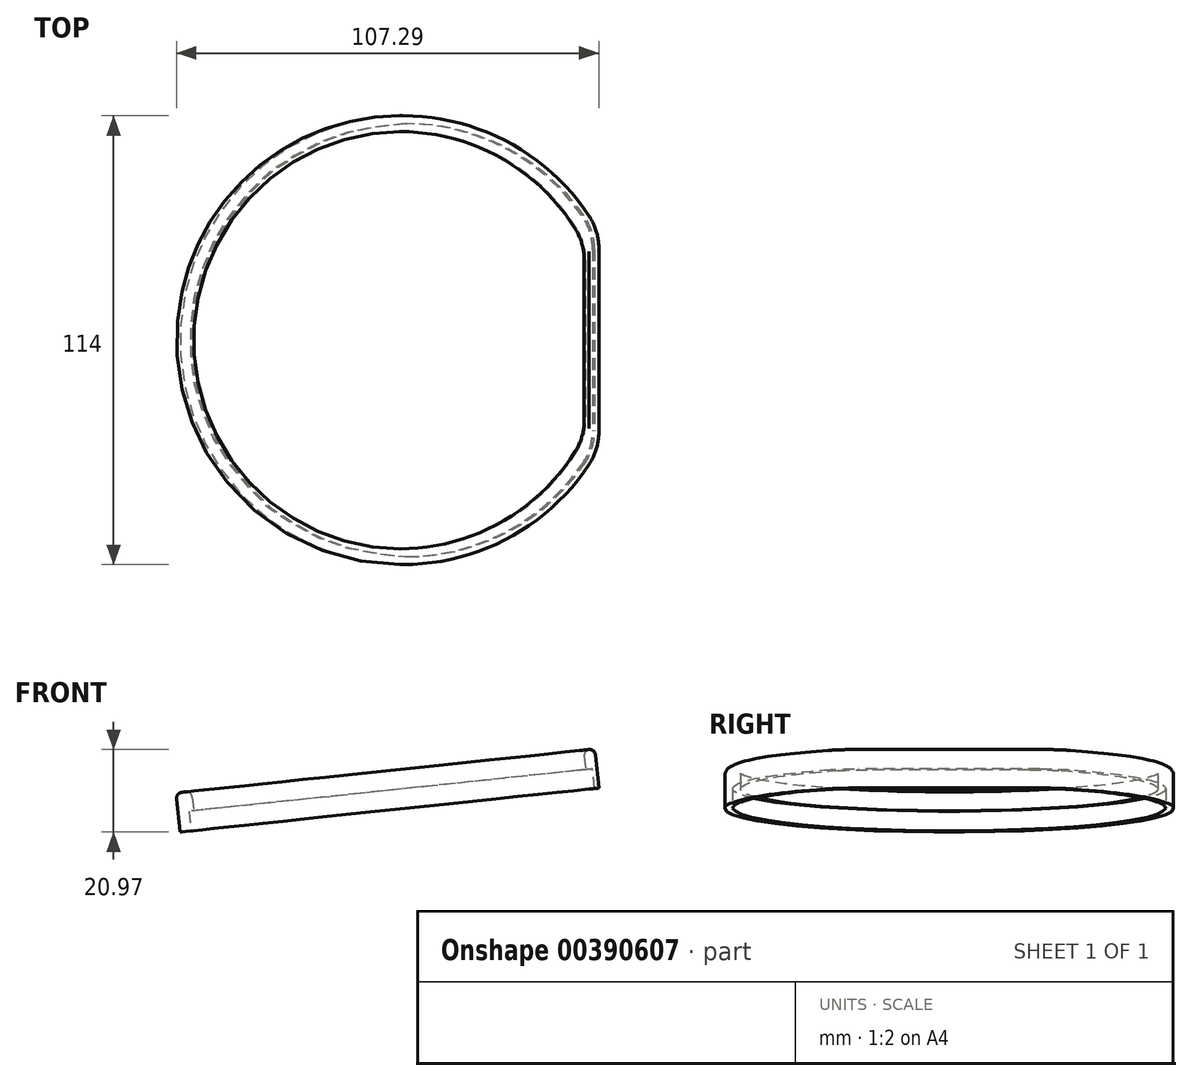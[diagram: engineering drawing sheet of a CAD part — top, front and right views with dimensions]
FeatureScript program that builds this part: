
annotation { "Feature Type Name" : "Feature", "Feature Type Description" : "" }
export const myFeature = defineFeature(function(context is Context, id is Id, definition is map)
    precondition{}
    {
        {
            var Q0;
            Q0=qCreatedBy(makeId("Front.planeOp"),FACE);
            var sketch = newSketch(context, id + "F0", { "sketchPlane" : qUnion([Q0])});
            skLineSegment(sketch, "E0", {"start": v(-46.94, 5.64) * mm, "end": v(44.02, 15.2) * mm, "construction": true});
            skLineSegment(sketch, "E1", {"start": v(-43.5, 0) * mm, "end": v(-43.5, 6) * mm, "construction": true});
            skLineSegment(sketch, "E2", {"start": v(43.5, 0) * mm, "end": v(43.5, 15.14) * mm, "construction": true});
            skLineSegment(sketch, "E3", {"start": v(-43.5, 0) * mm, "end": v(43.5, 0) * mm});
            skSolve(sketch);
        }
        {
            var Q0;
            Q0=sQuery(id+"F0.wireOp",EDGE,"E0");
            cPlane(context, id + "F1", {"entities" : qUnion([Q0]), "cplaneType" : CPlaneType.LINE_ANGLE, "offset" : 25 * mm, "angle" : 90 * degree, "width" : 150 * mm, "height" : 150 * mm});
        }
        {
            var Q0;
            Q0=qCreatedBy(id+"F1.planeOp",FACE);
            var sketch = newSketch(context, id + "F2", { "sketchPlane" : qUnion([Q0])});
            skCircle(sketch, "E4", {"center": v(0, 0) * mm, "radius": 53 * mm});
            skPoint(sketch, "E5", {"position": v(1, 0) * mm});
            skEllipse(sketch, "E6", {"center": v(1, 0) * mm, "majorRadius": 55.01 * mm, "minorRadius": 55.2 * mm, "majorAxis": v(0, 1)});
            skCircle(sketch, "E7", {"center": v(0, 0) * mm, "radius": 57 * mm});
            skLineSegment(sketch, "E8", {"start": v(48.86, 27.42) * mm, "end": v(48.86, -27.42) * mm});
            skLineSegment(sketch, "E9", {"start": v(47.12, 24.26) * mm, "end": v(47.12, -24.26) * mm});
            skLineSegment(sketch, "E10", {"start": v(49.98, -27.4) * mm, "end": v(49.98, 27.4) * mm});
            skSolve(sketch);
        }
        {
            var Q0;
            {var subQ4=sQuery(id+"F2.wireOp",EDGE,"E8");var subQ5=sQuery(id+"F2.wireOp",EDGE,"E6");var subQ7=makeQuery(id+"F2.imprint","INTERSECT",VERTEX,{"disambiguationData":[OD(1.0)],"derivedFrom":[subQ5,subQ4]});Q0=makeQuery(id+"F2.imprint","IMPRINT",FACE,{"disambiguationData":[TD([[makeQuery(id+"F2.imprint","IMPRINT",EDGE,{"disambiguationData":[TD([[subQ7,-1.0]])],"derivedFrom":subQ5}),-1.0]])]});}
            var Q1;
            {var subQ4=sQuery(id+"F2.wireOp",EDGE,"E9");var subQ5=sQuery(id+"F2.wireOp",EDGE,"E4");var subQ8=makeQuery(id+"F2.imprint","INTERSECT",VERTEX,{"disambiguationData":[OD(0.0)],"derivedFrom":[subQ5,subQ4]});Q1=makeQuery(id+"F2.imprint","IMPRINT",FACE,{"disambiguationData":[TD([[makeQuery(id+"F2.imprint","IMPRINT",EDGE,{"disambiguationData":[TD([[subQ8,1.0]])],"derivedFrom":subQ5}),-1.0]])]});}
            var Q2;
            {var subQ0=sQuery(id+"F2.wireOp",EDGE,"E9");Q2=makeQuery(id+"F2.imprint","IMPRINT",FACE,{"disambiguationData":[TD([[makeQuery(id+"F2.imprint","IMPRINT",EDGE,{"derivedFrom":subQ0}),1.0]])]});}
            var Q3;
            {var subQ0=sQuery(id+"F2.wireOp",EDGE,"E8");var subQ1=sQuery(id+"F2.wireOp",EDGE,"E4");var subQ2=makeQuery(id+"F2.imprint","INTERSECT",VERTEX,{"disambiguationData":[OD(0.0)],"derivedFrom":[subQ1,subQ0]});Q3=makeQuery(id+"F2.imprint","IMPRINT",FACE,{"disambiguationData":[TD([[makeQuery(id+"F2.imprint","IMPRINT",EDGE,{"disambiguationData":[TD([[subQ2,1.0]])],"derivedFrom":subQ1}),1.0]])]});}
            var Q4;
            {var subQ0=sQuery(id+"F2.wireOp",EDGE,"E8");var subQ1=sQuery(id+"F2.wireOp",EDGE,"E4");var subQ2=makeQuery(id+"F2.imprint","INTERSECT",VERTEX,{"disambiguationData":[OD(0.0)],"derivedFrom":[subQ1,subQ0]});Q4=makeQuery(id+"F2.imprint","IMPRINT",FACE,{"disambiguationData":[TD([[makeQuery(id+"F2.imprint","IMPRINT",EDGE,{"disambiguationData":[TD([[subQ2,1.0]])],"derivedFrom":subQ1}),-1.0]])]});}
            var Q5;
            {var subQ0=sQuery(id+"F2.wireOp",EDGE,"E8");var subQ1=sQuery(id+"F2.wireOp",EDGE,"E4");var subQ2=makeQuery(id+"F2.imprint","INTERSECT",VERTEX,{"disambiguationData":[OD(1.0)],"derivedFrom":[subQ1,subQ0]});Q5=makeQuery(id+"F2.imprint","IMPRINT",FACE,{"disambiguationData":[TD([[makeQuery(id+"F2.imprint","IMPRINT",EDGE,{"disambiguationData":[TD([[subQ2,-1.0]])],"derivedFrom":subQ1}),-1.0]])]});}
            extrude(context, id + "F3", {"entities" : qUnion([Q0, Q1, Q2, Q3, Q4, Q5]), "depth" : 5 * mm});
        }
        {
            var Q0;
            {var subQ4=sQuery(id+"F2.wireOp",EDGE,"E8");var subQ5=sQuery(id+"F2.wireOp",EDGE,"E6");var subQ7=makeQuery(id+"F2.imprint","INTERSECT",VERTEX,{"disambiguationData":[OD(1.0)],"derivedFrom":[subQ5,subQ4]});Q0=makeQuery(id+"F2.imprint","IMPRINT",FACE,{"disambiguationData":[TD([[makeQuery(id+"F2.imprint","IMPRINT",EDGE,{"disambiguationData":[TD([[subQ7,-1.0]])],"derivedFrom":subQ5}),-1.0]])]});}
            var Q1;
            {var subQ0=sQuery(id+"F2.wireOp",EDGE,"E8");var subQ1=sQuery(id+"F2.wireOp",EDGE,"E4");var subQ2=makeQuery(id+"F2.imprint","INTERSECT",VERTEX,{"disambiguationData":[OD(1.0)],"derivedFrom":[subQ1,subQ0]});Q1=makeQuery(id+"F2.imprint","IMPRINT",FACE,{"disambiguationData":[TD([[makeQuery(id+"F2.imprint","IMPRINT",EDGE,{"disambiguationData":[TD([[subQ2,-1.0]])],"derivedFrom":subQ1}),-1.0]])]});}
            var Q2;
            {var subQ0=sQuery(id+"F2.wireOp",EDGE,"E8");var subQ1=sQuery(id+"F2.wireOp",EDGE,"E4");var subQ2=makeQuery(id+"F2.imprint","INTERSECT",VERTEX,{"disambiguationData":[OD(0.0)],"derivedFrom":[subQ1,subQ0]});Q2=makeQuery(id+"F2.imprint","IMPRINT",FACE,{"disambiguationData":[TD([[makeQuery(id+"F2.imprint","IMPRINT",EDGE,{"disambiguationData":[TD([[subQ2,1.0]])],"derivedFrom":subQ1}),-1.0]])]});}
            var Q3;
            {var subQ0=sQuery(id+"F2.wireOp",EDGE,"E8");var subQ1=sQuery(id+"F2.wireOp",EDGE,"E4");var subQ2=makeQuery(id+"F2.imprint","INTERSECT",VERTEX,{"disambiguationData":[OD(0.0)],"derivedFrom":[subQ1,subQ0]});Q3=makeQuery(id+"F2.imprint","IMPRINT",FACE,{"disambiguationData":[TD([[makeQuery(id+"F2.imprint","IMPRINT",EDGE,{"disambiguationData":[TD([[subQ2,1.0]])],"derivedFrom":subQ1}),1.0]])]});}
            extrude(context, id + "F4", {"entities" : qUnion([Q0, Q1, Q2, Q3]), "operationType" : NewBodyOperationType.ADD, "oppositeDirection" : true, "depth" : 5 * mm});
        }
        {
            var Q0;
            {var subQ0=sQuery(id+"F2.wireOp",EDGE,"E9");var subQ1=sQuery(id+"F2.wireOp",EDGE,"E4");Q0=makeQuery(id+"F3.opExtrude","SWEPT_EDGE",EDGE,{"disambiguationData":[OSD([subQ1,subQ0]),TDD([makeQuery(id+"F2.imprint","INTERSECT",VERTEX,{"disambiguationData":[OD(0.0)],"derivedFrom":[subQ1,subQ0]})])]});}
            var Q1;
            {var subQ0=sQuery(id+"F2.wireOp",EDGE,"E9");var subQ1=sQuery(id+"F2.wireOp",EDGE,"E4");Q1=makeQuery(id+"F3.opExtrude","SWEPT_EDGE",EDGE,{"disambiguationData":[OSD([subQ1,subQ0]),TDD([makeQuery(id+"F2.imprint","INTERSECT",VERTEX,{"disambiguationData":[OD(1.0)],"derivedFrom":[subQ1,subQ0]})])]});}
            var Q2;
            {var subQ0=sQuery(id+"F2.wireOp",EDGE,"E8");var subQ1=sQuery(id+"F2.wireOp",EDGE,"E6");Q2=makeQuery(id+"F4.opExtrude","SWEPT_EDGE",EDGE,{"disambiguationData":[OSD([subQ1,subQ0]),TDD([makeQuery(id+"F2.imprint","INTERSECT",VERTEX,{"disambiguationData":[OD(1.0)],"derivedFrom":[subQ1,subQ0]})])]});}
            var Q3;
            {var subQ0=sQuery(id+"F2.wireOp",EDGE,"E8");var subQ1=sQuery(id+"F2.wireOp",EDGE,"E6");Q3=makeQuery(id+"F4.opExtrude","SWEPT_EDGE",EDGE,{"disambiguationData":[OSD([subQ1,subQ0]),TDD([makeQuery(id+"F2.imprint","INTERSECT",VERTEX,{"disambiguationData":[OD(0.0)],"derivedFrom":[subQ1,subQ0]})])]});}
            var Q4;
            {var subQ0=sQuery(id+"F2.wireOp",EDGE,"YyRSWi47-WFlA-Qzv6-HhTL-FOEKywX9Ik5g");var subQ1=sQuery(id+"F2.wireOp",EDGE,"E7");var subQ2=makeQuery(id+"F2.imprint","INTERSECT",VERTEX,{"disambiguationData":[OD(0.0)],"derivedFrom":[subQ1,subQ0]});Q4=makeQuery(id+"F4.boolean.opBoolean","MERGE",EDGE,{"derivedFrom":[makeQuery(id+"F3.opExtrude","SWEPT_EDGE",EDGE,{"disambiguationData":[OSD([subQ1,subQ0]),TDD([subQ2])]}),makeQuery(id+"F4.opExtrude","SWEPT_EDGE",EDGE,{"disambiguationData":[OSD([subQ1,subQ0]),TDD([subQ2])]})]});}
            var Q5;
            {var subQ0=sQuery(id+"F2.wireOp",EDGE,"YyRSWi47-WFlA-Qzv6-HhTL-FOEKywX9Ik5g");var subQ1=sQuery(id+"F2.wireOp",EDGE,"E7");var subQ2=makeQuery(id+"F2.imprint","INTERSECT",VERTEX,{"disambiguationData":[OD(1.0)],"derivedFrom":[subQ1,subQ0]});Q5=makeQuery(id+"F4.boolean.opBoolean","MERGE",EDGE,{"derivedFrom":[makeQuery(id+"F3.opExtrude","SWEPT_EDGE",EDGE,{"disambiguationData":[OSD([subQ1,subQ0]),TDD([subQ2])]}),makeQuery(id+"F4.opExtrude","SWEPT_EDGE",EDGE,{"disambiguationData":[OSD([subQ1,subQ0]),TDD([subQ2])]})]});}
            fillet(context, id + "F5", {"entities" : qUnion([Q0, Q1, Q2, Q3, Q4, Q5]), "radius" : 15 * mm, "tangentPropagation" : true, "allowEdgeOverflow" : false});
        }
        {
            var Q0;
            Q0=makeQuery(id+"F3.opExtrude","CAP_EDGE",EDGE,{"disambiguationData":[OSD([sQuery(id+"F2.wireOp",EDGE,"E7")])],"isStart":false});
            var Q1;
            Q1=makeQuery(id+"F3.opExtrude","CAP_EDGE",EDGE,{"disambiguationData":[OSD([sQuery(id+"F2.wireOp",EDGE,"E4")])],"isStart":false});
            fillet(context, id + "F6", {"entities" : qUnion([Q0, Q1]), "radius" : 1.5 * mm, "tangentPropagation" : true, "allowEdgeOverflow" : false});
        }
    });
